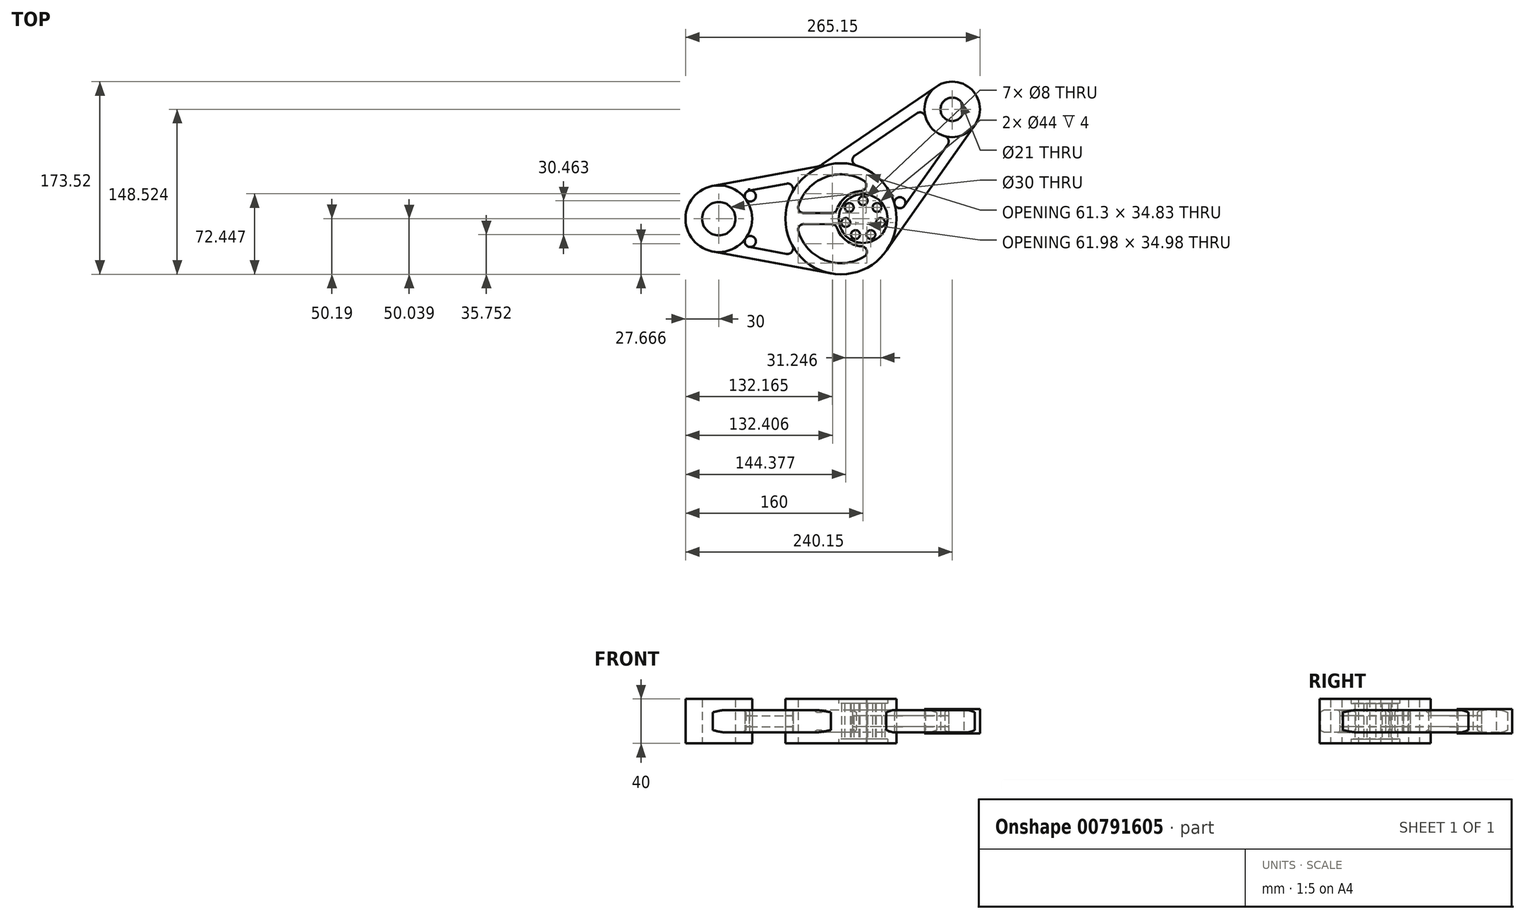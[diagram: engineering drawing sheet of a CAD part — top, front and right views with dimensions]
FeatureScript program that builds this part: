
annotation { "Feature Type Name" : "Feature", "Feature Type Description" : "" }
export const myFeature = defineFeature(function(context is Context, id is Id, definition is map)
    precondition{}
    {
        {
            var Q0;
            Q0=qCreatedBy(makeId("Top.planeOp"),FACE);
            var sketch = newSketch(context, id + "F0", { "sketchPlane" : qUnion([Q0])});
            skCircle(sketch, "E0", {"center": v(80.15, 98.33) * mm, "radius": 10.5 * mm});
            skCircle(sketch, "E1", {"center": v(80.15, 98.33) * mm, "radius": 25 * mm});
            skCircle(sketch, "E2", {"center": v(0, 0) * mm, "radius": 22 * mm});
            skCircle(sketch, "E3", {"center": v(-130, -0.15) * mm, "radius": 15 * mm});
            skCircle(sketch, "E4", {"center": v(-130, -0.15) * mm, "radius": 30 * mm});
            skCircle(sketch, "E5", {"center": v(-20, -0.2) * mm, "radius": 50 * mm});
            skPoint(sketch, "E6.start.orphan", {"position": v(0, 68.7) * mm});
            skLineSegment(sketch, "E7", {"start": v(-135.47, -29.65) * mm, "end": v(-29.11, -49.35) * mm});
            skLineSegment(sketch, "E8", {"start": v(-135.44, 29.35) * mm, "end": v(-41.94, 46.6) * mm});
            skLineSegment(sketch, "E9", {"start": v(66.07, 119) * mm, "end": v(-37.36, 48.5) * mm});
            skArc(sketch, "E10", {"start": v(-41.94, 46.6) * mm, "mid": v(-39.55, 47.3) * mm, "end": v(-37.36, 48.5) * mm});
            skLineSegment(sketch, "E11", {"start": v(100.57, 83.92) * mm, "end": v(20.84, -29.03) * mm});
            skLineSegment(sketch, "E12", {"start": v(0, 0) * mm, "end": v(0, 16.02) * mm, "construction": true});
            skCircle(sketch, "E13", {"center": v(0, 16.02) * mm, "radius": 4 * mm});
            skCircle(sketch, "E14.1.0", {"center": v(-12.53, 10) * mm, "radius": 4 * mm});
            skCircle(sketch, "E14.2.0", {"center": v(-15.62, -3.57) * mm, "radius": 4 * mm});
            skCircle(sketch, "E15.1.3.0", {"center": v(-6.95, -14.44) * mm, "radius": 4 * mm});
            skCircle(sketch, "E15.1.4.0", {"center": v(6.95, -14.44) * mm, "radius": 4 * mm});
            skCircle(sketch, "E15.1.5.0", {"center": v(15.62, -3.57) * mm, "radius": 4 * mm});
            skCircle(sketch, "E15.1.6.0", {"center": v(12.53, 10) * mm, "radius": 4 * mm});
            skLineSegment(sketch, "E16.0", {"start": v(-111.66, -23.9) * mm, "end": v(-56.79, -34.06) * mm});
            skLineSegment(sketch, "E17.0", {"start": v(-111.64, 23.57) * mm, "end": v(-56.76, 33.7) * mm});
            skLineSegment(sketch, "E18.0", {"start": v(55.18, 99.46) * mm, "end": v(-17.74, 49.76) * mm});
            skLineSegment(sketch, "E19.0", {"start": v(80.87, 73.34) * mm, "end": v(29.98, 1.25) * mm});
            skArc(sketch, "E20", {"start": v(-102.39, 25.28) * mm, "mid": v(-106.24, 22.27) * mm, "end": v(-105.68, 17.41) * mm});
            skPoint(sketch, "E20.first.point", {"position": v(-102.68, 25.23) * mm});
            skPoint(sketch, "E20.second.point", {"position": v(-105.68, 17.41) * mm});
            skPoint(sketch, "E20.third.point", {"position": v(-96.63, 20.28) * mm});
            skArc(sketch, "E21", {"start": v(-63.7, 24.1) * mm, "mid": v(-64.02, 29.45) * mm, "end": v(-68.98, 31.45) * mm});
            skArc(sketch, "E22", {"start": v(-105.7, -17.73) * mm, "mid": v(-106.28, -22.52) * mm, "end": v(-102.55, -25.58) * mm});
            skArc(sketch, "E23", {"start": v(-69, -31.8) * mm, "mid": v(-64.04, -29.8) * mm, "end": v(-63.72, -24.45) * mm});
            skArc(sketch, "E24", {"start": v(-7.48, 56.76) * mm, "mid": v(-9.6, 51.84) * mm, "end": v(-6.06, 47.82) * mm});
            skArc(sketch, "E25", {"start": v(55.98, 91.94) * mm, "mid": v(52.9, 95.35) * mm, "end": v(48.33, 94.8) * mm});
            skArc(sketch, "E26", {"start": v(76.1, 66.58) * mm, "mid": v(76.72, 71.13) * mm, "end": v(73.37, 74.27) * mm});
            skArc(sketch, "E27", {"start": v(28.23, 12.97) * mm, "mid": v(32.2, 9.36) * mm, "end": v(37.14, 11.4) * mm});
            skArc(sketch, "E28", {"start": v(0.38, 34.22) * mm, "mid": v(-34.5, 37.1) * mm, "end": v(-58.28, 11.42) * mm});
            skLineSegment(sketch, "E29.0", {"start": v(-60.03, -5) * mm, "end": v(-59.71, -5) * mm});
            skLineSegment(sketch, "E30.0", {"start": v(-53.52, 4.97) * mm, "end": v(-28.37, 4.84) * mm});
            skArc(sketch, "E31", {"start": v(-1.8, 24.93) * mm, "mid": v(-15.22, 19.84) * mm, "end": v(-23.62, 8.2) * mm});
            skArc(sketch, "E32", {"start": v(-58.28, 11.42) * mm, "mid": v(-57.52, 7) * mm, "end": v(-53.52, 4.97) * mm});
            skArc(sketch, "E33", {"start": v(-1.8, 24.93) * mm, "mid": v(2.7, 28.78) * mm, "end": v(0.38, 34.22) * mm});
            skArc(sketch, "E34", {"start": v(-28.37, 4.84) * mm, "mid": v(-25.45, 5.76) * mm, "end": v(-23.62, 8.2) * mm});
            skArc(sketch, "E35", {"start": v(-53.57, -5.03) * mm, "mid": v(-57.59, -7.02) * mm, "end": v(-58.39, -11.44) * mm});
            skArc(sketch, "E36", {"start": v(-23.52, -8.47) * mm, "mid": v(-25.34, -6.08) * mm, "end": v(-28.2, -5.16) * mm});
            skArc(sketch, "E37", {"start": v(1.04, -34.21) * mm, "mid": v(3.25, -28.72) * mm, "end": v(-1.33, -24.96) * mm});
            skArc(sketch, "E38.trimOffspring", {"start": v(-58.39, -11.44) * mm, "mid": v(-34.32, -37.54) * mm, "end": v(1.04, -34.21) * mm});
            skLineSegment(sketch, "E39.trimOffspring", {"start": v(-53.57, -5.03) * mm, "end": v(-28.2, -5.16) * mm});
            skPoint(sketch, "E40.orphan", {"position": v(-60, 0) * mm});
            skArc(sketch, "E41.trimOffspring", {"start": v(-23.52, -8.47) * mm, "mid": v(-14.91, -20.06) * mm, "end": v(-1.33, -24.96) * mm});
            skPoint(sketch, "E42.orphan", {"position": v(-21.47, 4.8) * mm});
            skPoint(sketch, "E43.end.orphan", {"position": v(-22, -0.2) * mm});
            skPoint(sketch, "E44.orphan", {"position": v(-21.38, -5.2) * mm});
            skSolve(sketch);
        }
        {
            var Q0;
            Q0=makeQuery(id+"F0.imprint","IMPRINT",FACE,{"disambiguationData":[TD([[makeQuery(id+"F0.imprint","IMPRINT",EDGE,{"derivedFrom":sQuery(id+"F0.wireOp",EDGE,"E3")}),-1.0]])]});
            extrude(context, id + "F1", {"entities" : qUnion([Q0]), "endBound" : BoundingType.SYMMETRIC, "depth" : 40 * mm, "offsetDistance" : 25.4 * mm});
        }
        {
            var Q0;
            Q0=makeQuery(id+"F0.imprint","IMPRINT",FACE,{"disambiguationData":[TD([[makeQuery(id+"F0.imprint","IMPRINT",EDGE,{"derivedFrom":sQuery(id+"F0.wireOp",EDGE,"E2")}),1.0]])]});
            extrude(context, id + "F2", {"entities" : qUnion([Q0]), "endBound" : BoundingType.SYMMETRIC, "depth" : 32 * mm, "offsetDistance" : 25.4 * mm});
        }
        {
            var Q0;
            Q0=makeQuery(id+"F0.imprint","IMPRINT",FACE,{"disambiguationData":[TD([[makeQuery(id+"F0.imprint","IMPRINT",EDGE,{"derivedFrom":sQuery(id+"F0.wireOp",EDGE,"E2")}),-1.0]])]});
            extrude(context, id + "F3", {"entities" : qUnion([Q0]), "operationType" : NewBodyOperationType.ADD, "endBound" : BoundingType.SYMMETRIC, "depth" : 40 * mm, "offsetDistance" : 25.4 * mm});
        }
        {
            var Q0;
            {var subQ10=sQuery(id+"F0.wireOp",EDGE,"E8");Q0=makeQuery(id+"F0.imprint","IMPRINT",FACE,{"disambiguationData":[TD([[makeQuery(id+"F0.imprint","IMPRINT",EDGE,{"derivedFrom":subQ10}),-1.0]])]});}
            var Q1;
            {var subQ4=sQuery(id+"F0.wireOp",EDGE,"E11");Q1=makeQuery(id+"F0.imprint","IMPRINT",FACE,{"disambiguationData":[TD([[makeQuery(id+"F0.imprint","IMPRINT",EDGE,{"derivedFrom":subQ4}),-1.0]])]});}
            var Q2;
            {var subQ0=sQuery(id+"F0.wireOp",EDGE,"E7");Q2=makeQuery(id+"F0.imprint","IMPRINT",FACE,{"disambiguationData":[TD([[makeQuery(id+"F0.imprint","IMPRINT",EDGE,{"derivedFrom":subQ0}),1.0]])]});}
            var Q3;
            {var subQ3=sQuery(id+"F0.wireOp",EDGE,"E21");Q3=makeQuery(id+"F0.imprint","IMPRINT",FACE,{"disambiguationData":[TD([[makeQuery(id+"F0.imprint","IMPRINT",EDGE,{"derivedFrom":subQ3}),-1.0]])]});}
            var Q4;
            {var subQ0=sQuery(id+"F0.wireOp",EDGE,"E17.0");var subQ1=sQuery(id+"F0.wireOp",EDGE,"E4");var subQ2=makeQuery(id+"F0.imprint","INTERSECT",VERTEX,{"derivedFrom":[subQ1,subQ0]});Q4=makeQuery(id+"F0.imprint","IMPRINT",FACE,{"disambiguationData":[TD([[makeQuery(id+"F0.imprint","IMPRINT",EDGE,{"disambiguationData":[TD([[subQ2,1.0]])],"derivedFrom":subQ1}),-1.0]])]});}
            var Q5;
            {var subQ3=sQuery(id+"F0.wireOp",EDGE,"E22");Q5=makeQuery(id+"F0.imprint","IMPRINT",FACE,{"disambiguationData":[TD([[makeQuery(id+"F0.imprint","IMPRINT",EDGE,{"derivedFrom":subQ3}),-1.0]])]});}
            var Q6;
            {var subQ3=sQuery(id+"F0.wireOp",EDGE,"E23");Q6=makeQuery(id+"F0.imprint","IMPRINT",FACE,{"disambiguationData":[TD([[makeQuery(id+"F0.imprint","IMPRINT",EDGE,{"derivedFrom":subQ3}),-1.0]])]});}
            var Q7;
            {var subQ3=sQuery(id+"F0.wireOp",EDGE,"E24");Q7=makeQuery(id+"F0.imprint","IMPRINT",FACE,{"disambiguationData":[TD([[makeQuery(id+"F0.imprint","IMPRINT",EDGE,{"derivedFrom":subQ3}),-1.0]])]});}
            var Q8;
            {var subQ3=sQuery(id+"F0.wireOp",EDGE,"E27");Q8=makeQuery(id+"F0.imprint","IMPRINT",FACE,{"disambiguationData":[TD([[makeQuery(id+"F0.imprint","IMPRINT",EDGE,{"derivedFrom":subQ3}),-1.0]])]});}
            var Q9;
            {var subQ3=sQuery(id+"F0.wireOp",EDGE,"E25");Q9=makeQuery(id+"F0.imprint","IMPRINT",FACE,{"disambiguationData":[TD([[makeQuery(id+"F0.imprint","IMPRINT",EDGE,{"derivedFrom":subQ3}),-1.0]])]});}
            var Q10;
            {var subQ3=sQuery(id+"F0.wireOp",EDGE,"E26");Q10=makeQuery(id+"F0.imprint","IMPRINT",FACE,{"disambiguationData":[TD([[makeQuery(id+"F0.imprint","IMPRINT",EDGE,{"derivedFrom":subQ3}),-1.0]])]});}
            extrude(context, id + "F4", {"entities" : qUnion([Q0, Q1, Q2, Q3, Q4, Q5, Q6, Q7, Q8, Q9, Q10]), "endBound" : BoundingType.SYMMETRIC, "depth" : 20 * mm, "offsetDistance" : 25.4 * mm});
        }
        {
            var Q0;
            Q0=makeQuery(id+"F0.imprint","IMPRINT",FACE,{"disambiguationData":[TD([[makeQuery(id+"F0.imprint","IMPRINT",EDGE,{"derivedFrom":sQuery(id+"F0.wireOp",EDGE,"E0")}),-1.0]])]});
            extrude(context, id + "F5", {"entities" : qUnion([Q0]), "endBound" : BoundingType.SYMMETRIC, "depth" : 22 * mm, "offsetDistance" : 25.4 * mm});
        }
        {
            var Q0;
            {var subQ4=sQuery(id+"F0.wireOp",EDGE,"E21");Q0=makeQuery(id+"F0.imprint","IMPRINT",FACE,{"disambiguationData":[TD([[makeQuery(id+"F0.imprint","IMPRINT",EDGE,{"derivedFrom":subQ4}),1.0]])]});}
            var Q1;
            {var subQ0=sQuery(id+"F0.wireOp",EDGE,"E24");Q1=makeQuery(id+"F0.imprint","IMPRINT",FACE,{"disambiguationData":[TD([[makeQuery(id+"F0.imprint","IMPRINT",EDGE,{"derivedFrom":subQ0}),1.0]])]});}
            extrude(context, id + "F6", {"entities" : qUnion([Q0, Q1]), "endBound" : BoundingType.SYMMETRIC, "depth" : 10 * mm, "offsetDistance" : 25.4 * mm});
        }
        {
            var Q0;
            Q0=makeQuery(id+"F4.opExtrude","CAP_EDGE",EDGE,{"disambiguationData":[OSD([sQuery(id+"F0.wireOp",EDGE,"E7")])],"isStart":false});
            fillet(context, id + "F7", {"entities" : qUnion([Q0]), "radius" : 2 * mm, "tangentPropagation" : true, "allowEdgeOverflow" : false});
        }
        {
            var Q0;
            Q0=makeQuery(id+"F4.opExtrude","CAP_EDGE",EDGE,{"disambiguationData":[OSD([sQuery(id+"F0.wireOp",EDGE,"E25")])],"isStart":false});
            var Q1;
            Q1=makeQuery(id+"F4.opExtrude","CAP_EDGE",EDGE,{"disambiguationData":[OSD([sQuery(id+"F0.wireOp",EDGE,"E26")])],"isStart":true});
            var Q2;
            Q2=makeQuery(id+"F4.opExtrude","CAP_EDGE",EDGE,{"disambiguationData":[OSD([sQuery(id+"F0.wireOp",EDGE,"E20")])],"isStart":true});
            var Q3;
            Q3=makeQuery(id+"F4.opExtrude","CAP_EDGE",EDGE,{"disambiguationData":[OSD([sQuery(id+"F0.wireOp",EDGE,"E11")])],"isStart":true});
            var Q4;
            Q4=makeQuery(id+"F4.opExtrude","CAP_EDGE",EDGE,{"disambiguationData":[OSD([sQuery(id+"F0.wireOp",EDGE,"E17.0")])],"isStart":false});
            var Q5;
            Q5=makeQuery(id+"F4.opExtrude","CAP_EDGE",EDGE,{"disambiguationData":[OSD([sQuery(id+"F0.wireOp",EDGE,"E19.0")])],"isStart":true});
            var Q6;
            Q6=makeQuery(id+"F4.opExtrude","CAP_EDGE",EDGE,{"disambiguationData":[OSD([sQuery(id+"F0.wireOp",EDGE,"E24")])],"isStart":true});
            var Q7;
            Q7=makeQuery(id+"F4.opExtrude","CAP_EDGE",EDGE,{"disambiguationData":[OSD([sQuery(id+"F0.wireOp",EDGE,"E8")])],"isStart":false});
            var Q8;
            Q8=makeQuery(id+"F4.opExtrude","CAP_EDGE",EDGE,{"disambiguationData":[OSD([sQuery(id+"F0.wireOp",EDGE,"E9")])],"isStart":true});
            var Q9;
            Q9=makeQuery(id+"F4.opExtrude","CAP_EDGE",EDGE,{"disambiguationData":[OSD([sQuery(id+"F0.wireOp",EDGE,"E18.0")])],"isStart":true});
            var Q10;
            Q10=makeQuery(id+"F4.opExtrude","CAP_EDGE",EDGE,{"disambiguationData":[OSD([sQuery(id+"F0.wireOp",EDGE,"E22")])],"isStart":false});
            var Q11;
            Q11=makeQuery(id+"F4.opExtrude","CAP_EDGE",EDGE,{"disambiguationData":[OSD([sQuery(id+"F0.wireOp",EDGE,"E26")])],"isStart":false});
            var Q12;
            Q12=makeQuery(id+"F4.opExtrude","CAP_EDGE",EDGE,{"disambiguationData":[OSD([sQuery(id+"F0.wireOp",EDGE,"E18.0")])],"isStart":false});
            var Q13;
            Q13=makeQuery(id+"F4.opExtrude","CAP_EDGE",EDGE,{"disambiguationData":[OSD([sQuery(id+"F0.wireOp",EDGE,"E21")])],"isStart":false});
            var Q14;
            Q14=makeQuery(id+"F4.opExtrude","CAP_EDGE",EDGE,{"disambiguationData":[OSD([sQuery(id+"F0.wireOp",EDGE,"E21")])],"isStart":true});
            var Q15;
            Q15=makeQuery(id+"F4.opExtrude","CAP_EDGE",EDGE,{"disambiguationData":[OSD([sQuery(id+"F0.wireOp",EDGE,"E8")])],"isStart":true});
            var Q16;
            Q16=makeQuery(id+"F4.opExtrude","CAP_EDGE",EDGE,{"disambiguationData":[OSD([sQuery(id+"F0.wireOp",EDGE,"E7")])],"isStart":true});
            var Q17;
            Q17=makeQuery(id+"F4.opExtrude","CAP_EDGE",EDGE,{"disambiguationData":[OSD([sQuery(id+"F0.wireOp",EDGE,"E22")])],"isStart":true});
            var Q18;
            Q18=makeQuery(id+"F4.opExtrude","CAP_EDGE",EDGE,{"disambiguationData":[OSD([sQuery(id+"F0.wireOp",EDGE,"E23")])],"isStart":false});
            var Q19;
            Q19=makeQuery(id+"F4.opExtrude","CAP_EDGE",EDGE,{"disambiguationData":[OSD([sQuery(id+"F0.wireOp",EDGE,"E23")])],"isStart":true});
            var Q20;
            Q20=makeQuery(id+"F4.opExtrude","CAP_EDGE",EDGE,{"disambiguationData":[OSD([sQuery(id+"F0.wireOp",EDGE,"E27")])],"isStart":true});
            var Q21;
            Q21=makeQuery(id+"F4.opExtrude","CAP_EDGE",EDGE,{"disambiguationData":[OSD([sQuery(id+"F0.wireOp",EDGE,"E9")])],"isStart":false});
            var Q22;
            Q22=makeQuery(id+"F4.opExtrude","CAP_EDGE",EDGE,{"disambiguationData":[OSD([sQuery(id+"F0.wireOp",EDGE,"E10")])],"isStart":false});
            var Q23;
            Q23=makeQuery(id+"F4.opExtrude","CAP_EDGE",EDGE,{"disambiguationData":[OSD([sQuery(id+"F0.wireOp",EDGE,"E10")])],"isStart":true});
            var Q24;
            Q24=makeQuery(id+"F4.opExtrude","CAP_EDGE",EDGE,{"disambiguationData":[OSD([sQuery(id+"F0.wireOp",EDGE,"E11")])],"isStart":false});
            var Q25;
            Q25=makeQuery(id+"F4.opExtrude","CAP_EDGE",EDGE,{"disambiguationData":[OSD([sQuery(id+"F0.wireOp",EDGE,"E24")])],"isStart":false});
            var Q26;
            Q26=makeQuery(id+"F4.opExtrude","CAP_EDGE",EDGE,{"disambiguationData":[OSD([sQuery(id+"F0.wireOp",EDGE,"E16.0")])],"isStart":true});
            var Q27;
            Q27=makeQuery(id+"F4.opExtrude","CAP_EDGE",EDGE,{"disambiguationData":[OSD([sQuery(id+"F0.wireOp",EDGE,"E16.0")])],"isStart":false});
            var Q28;
            Q28=makeQuery(id+"F4.opExtrude","CAP_EDGE",EDGE,{"disambiguationData":[OSD([sQuery(id+"F0.wireOp",EDGE,"E20")])],"isStart":false});
            var Q29;
            Q29=makeQuery(id+"F4.opExtrude","CAP_EDGE",EDGE,{"disambiguationData":[OSD([sQuery(id+"F0.wireOp",EDGE,"E27")])],"isStart":false});
            var Q30;
            Q30=makeQuery(id+"F4.opExtrude","CAP_EDGE",EDGE,{"disambiguationData":[OSD([sQuery(id+"F0.wireOp",EDGE,"E17.0")])],"isStart":true});
            var Q31;
            Q31=makeQuery(id+"F4.opExtrude","CAP_EDGE",EDGE,{"disambiguationData":[OSD([sQuery(id+"F0.wireOp",EDGE,"E19.0")])],"isStart":false});
            var Q32;
            Q32=makeQuery(id+"F4.opExtrude","CAP_EDGE",EDGE,{"disambiguationData":[OSD([sQuery(id+"F0.wireOp",EDGE,"E25")])],"isStart":true});
            fillet(context, id + "F8", {"entities" : qUnion([Q0, Q1, Q2, Q3, Q4, Q5, Q6, Q7, Q8, Q9, Q10, Q11, Q12, Q13, Q14, Q15, Q16, Q17, Q18, Q19, Q20, Q21, Q22, Q23, Q24, Q25, Q26, Q27, Q28, Q29, Q30, Q31, Q32]), "radius" : 2 * mm, "tangentPropagation" : true, "allowEdgeOverflow" : false});
        }
    });
